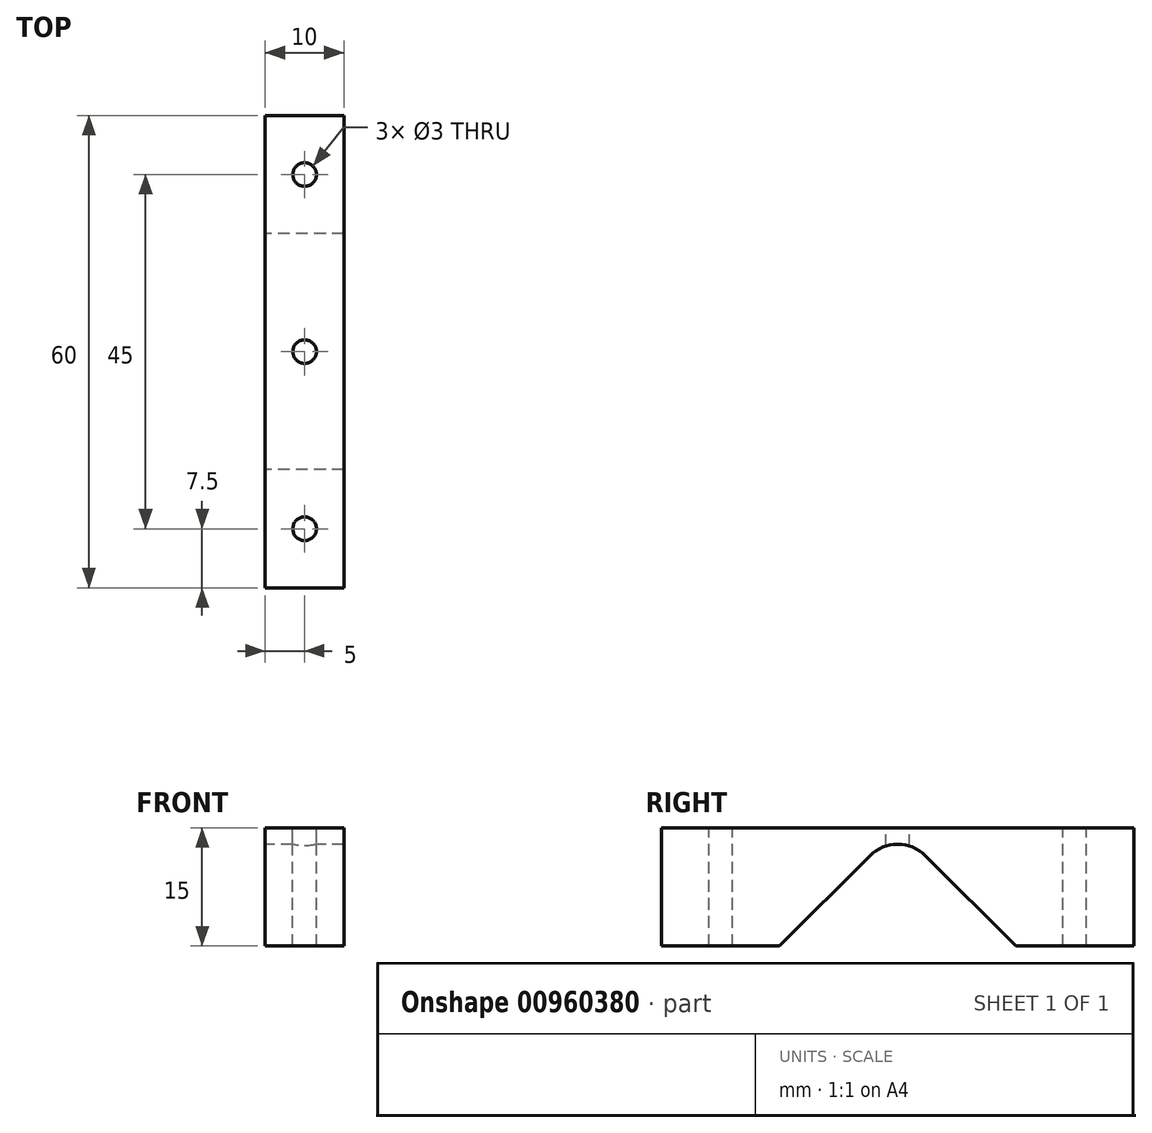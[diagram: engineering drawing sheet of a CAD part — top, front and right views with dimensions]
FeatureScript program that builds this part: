
annotation { "Feature Type Name" : "Feature", "Feature Type Description" : "" }
export const myFeature = defineFeature(function(context is Context, id is Id, definition is map)
    precondition{}
    {
        {
            var Q0;
            Q0=qCreatedBy(makeId("Right.planeOp"),FACE);
            var sketch = newSketch(context, id + "F0", { "sketchPlane" : qUnion([Q0])});
            skLineSegment(sketch, "E0.top", {"start": v(-30, 15) * mm, "end": v(30, 15) * mm});
            skLineSegment(sketch, "E0.left", {"start": v(-30, 0) * mm, "end": v(-30, 15) * mm});
            skLineSegment(sketch, "E0.right", {"start": v(30, 0) * mm, "end": v(30, 15) * mm});
            skLineSegment(sketch, "E1", {"start": v(-30, 0) * mm, "end": v(-15, 0) * mm});
            skLineSegment(sketch, "E2", {"start": v(-15, 0) * mm, "end": v(-3.54, 11.46) * mm});
            skLineSegment(sketch, "E3", {"start": v(3.54, 11.46) * mm, "end": v(15, 0) * mm});
            skLineSegment(sketch, "E4", {"start": v(15, 0) * mm, "end": v(30, 0) * mm});
            skPoint(sketch, "E5.visualSharp", {"position": v(0, 15) * mm});
            skArc(sketch, "E5.filletArc", {"start": v(3.54, 11.46) * mm, "mid": v(0, 12.93) * mm, "end": v(-3.54, 11.46) * mm});
            skSolve(sketch);
        }
        {
            var Q0;
            Q0=qSketchRegion(id+"F0",true);
            extrude(context, id + "F1", {"entities" : qUnion([Q0]), "depth" : 10 * mm, "offsetDistance" : 25 * mm});
        }
        {
            var Q0;
            Q0=makeQuery(id+"F1.opExtrude","SWEPT_FACE",FACE,{"disambiguationData":[OSD([sQuery(id+"F0.wireOp",EDGE,"E0.top")])]});
            var sketch = newSketch(context, id + "F2", { "sketchPlane" : qUnion([Q0])});
            skCircle(sketch, "E6", {"center": v(5, 0) * mm, "radius": 1.5 * mm});
            skCircle(sketch, "E7", {"center": v(5, 22.5) * mm, "radius": 1.5 * mm});
            skPoint(sketch, "E7.centerSnap0", {"position": v(5, 30) * mm});
            skCircle(sketch, "E8", {"center": v(5, -22.5) * mm, "radius": 1.5 * mm});
            skPoint(sketch, "E8.centerSnap0", {"position": v(5, -30) * mm});
            skSolve(sketch);
        }
        {
            var Q0;
            Q0=qSketchRegion(id+"F2",true);
            extrude(context, id + "F3", {"entities" : qUnion([Q0]), "operationType" : NewBodyOperationType.REMOVE, "endBound" : BoundingType.UP_TO_NEXT, "oppositeDirection" : true, "depth" : 25 * mm, "offsetDistance" : 25 * mm});
        }
    });
